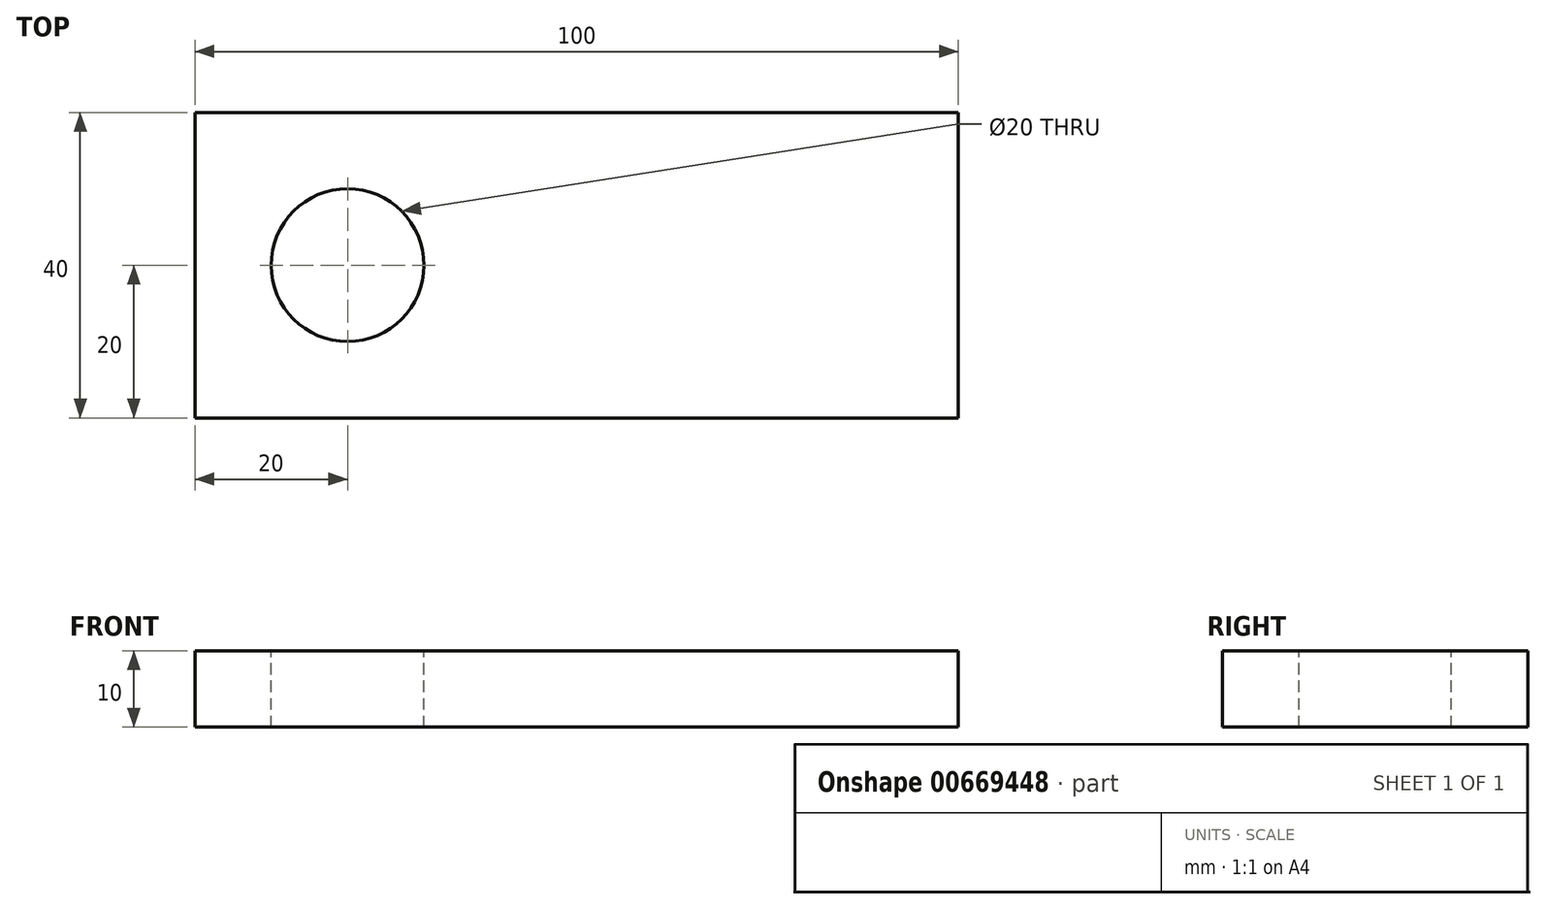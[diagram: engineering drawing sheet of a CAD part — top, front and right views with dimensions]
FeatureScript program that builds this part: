
annotation { "Feature Type Name" : "Feature", "Feature Type Description" : "" }
export const myFeature = defineFeature(function(context is Context, id is Id, definition is map)
    precondition{}
    {
        {
            var Q0;
            Q0=qCreatedBy(makeId("Top.planeOp"),FACE);
            var sketch = newSketch(context, id + "F0", { "sketchPlane" : qUnion([Q0])});
            skLineSegment(sketch, "E0.bottom", {"start": v(-96.85, 55.9) * mm, "end": v(3.15, 55.9) * mm});
            skLineSegment(sketch, "E0.top", {"start": v(-96.85, 15.9) * mm, "end": v(3.15, 15.9) * mm});
            skLineSegment(sketch, "E0.left", {"start": v(-96.85, 55.9) * mm, "end": v(-96.85, 15.9) * mm});
            skLineSegment(sketch, "E0.right", {"start": v(3.15, 55.9) * mm, "end": v(3.15, 15.9) * mm});
            skCircle(sketch, "E1", {"center": v(-76.85, 35.9) * mm, "radius": 10 * mm});
            skSolve(sketch);
        }
        {
            var Q0;
            Q0=makeQuery(id+"F0.imprint","IMPRINT",FACE,{"disambiguationData":[TD([[makeQuery(id+"F0.imprint","IMPRINT",EDGE,{"derivedFrom":sQuery(id+"F0.wireOp",EDGE,"E0.bottom")}),-1.0]])]});
            extrude(context, id + "F1", {"entities" : qUnion([Q0]), "oppositeDirection" : true, "depth" : 10 * mm, "offsetDistance" : 25 * mm});
        }
    });
